# Revit family: CU2
name_source: partatom
category: Lighting Fixtures
units: mm (PartAtom-declared; Revit-internal decimal feet)

## family parameters
Cut with Voids When Loaded = No
Host = Face
Light Source = No
OmniClass Number = 23.80.70.11.21
OmniClass Title = Emergency Lighting
Part Type = Normal
Room Calculation Point = No
Round Connector Dimension = Use Diameter
Shared = No

## types (4) — shared parameters
120 Voltage = Yes
277 Voltage = No
Apparent Load = 1 VA
Default Elevation = 48.000"
Lamp = LED Lamp
Lens = Glass 2
Load Classification = Lighting
Manufacturer = Compass Products
URL = https://www.currentlighting.com
Voltage = 120 V
Wattage Comments = 1 W
zz Watts 1 = 1 W
zz Watts 2 = 1 W

## per-type parameters (varying)
| type | Description | Finish | zz Integer 1 |
| CU2 | White Thermoplastic, Dual-Head LED Emergency Light , 120/277 Input, Damp Location Listed, 3 VDC, 1 Watt | White | 1 |
| CU2B | Black Thermoplastic, Dual-Head LED Emergancy Light, 120/277 Input, Damp Location Listed, 3 VDC, 1 Watt | Black | 1 |
| CU2RC | White Thermoplastic, Dual-Head LED Emergency Light, 120/277 Input, Damp Location Listed, Remote Capacity, 3VDC, 1Watt | White | 2 |
| CU2RCB | Black Thermoplastic, Dual-Head LED Emergency Light, 120/277 Input, Damp Location Listed, Remote Capacity, 3VDC, 1Watt | Black | 2 |

note: column(s) folded — value = type name in every type: Model

## geometry (parser evidence)
native form markers: Blend x11, Sweep x8
no freeform markers — native parametric forms only
